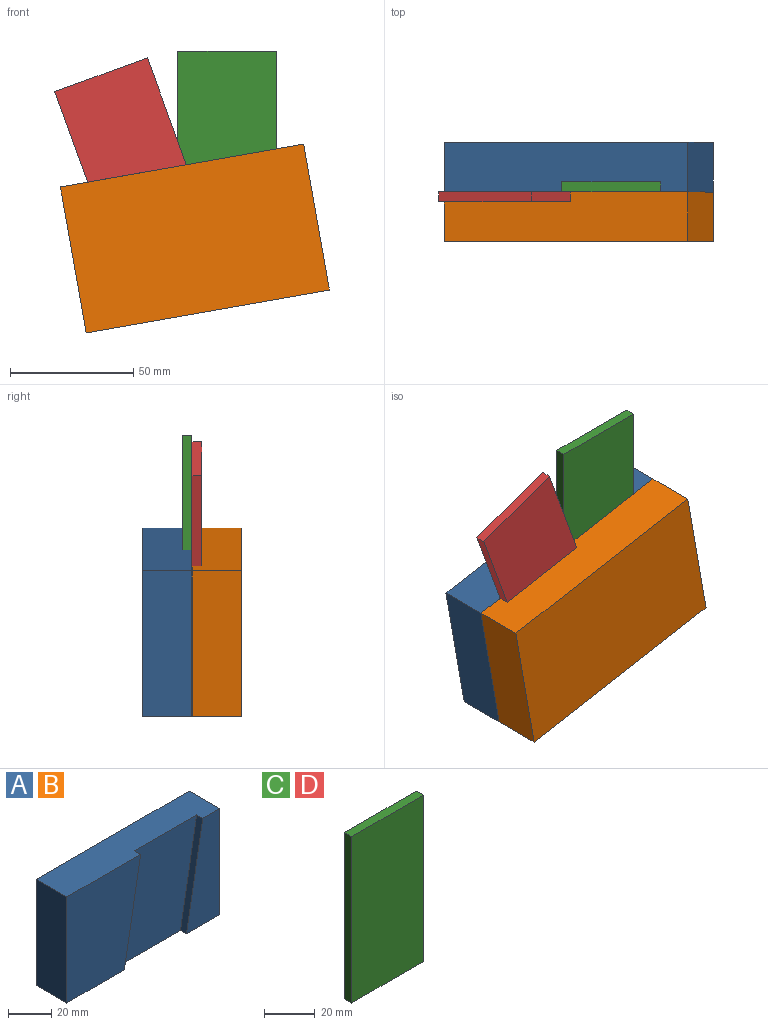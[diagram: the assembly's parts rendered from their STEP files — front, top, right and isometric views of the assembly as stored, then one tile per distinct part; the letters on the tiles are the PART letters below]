
ASSEMBLY  parts=4 mates=7
PART A: 10 faces, bbox 100x20x60 mm
  f0: plane 60x21.73mm, normal (0,-1,0), area 986.2mm2, adj f2,f4,f5,f7
  f1: plane 60x48.24mm, normal (0,-1,0), area 2576.8mm2, adj f2,f3,f4,f8
  f2: plane 100x20mm, normal (0,0,1), area 1837.5mm2, adj f0,f1,f3,f5,f6,f7,f8,f9
  f3: plane 60x20mm, normal (-1,0,0), area 1200mm2, adj f1,f2,f4,f6
  f4: plane 100x20mm, normal (0,0,-1), area 1837.5mm2, adj f0,f1,f3,f5,f6,f7,f8,f9
  f5: plane 60x20mm, normal (1,0,0), area 1200mm2, adj f0,f2,f4,f6
  f6: plane 100x60mm, normal (0,1,0), area 6000mm2, adj f2,f3,f4,f5
  f7: plane 60x10.58mm, normal (-0.98,0,0.17), area 243.7mm2, adj f0,f2,f4,f9
  f8: plane 60x10.58mm, normal (0.98,0,-0.17), area 243.7mm2, adj f1,f2,f4,f9
  f9: plane 60x51.2mm, normal (0,-1,0), area 2437mm2, adj f2,f4,f7,f8
PART B: same geometry as A
PART C: 6 faces, bbox 40x4x80 mm
  f0: plane 80x4mm, normal (-1,0,0), area 320mm2, adj f1,f3,f4,f5
  f1: plane 40x4mm, normal (0,0,-1), area 160mm2, adj f0,f2,f4,f5
  f2: plane 80x4mm, normal (1,0,0), area 320mm2, adj f1,f3,f4,f5
  f3: plane 40x4mm, normal (0,0,1), area 160mm2, adj f0,f2,f4,f5
  f4: plane 80x40mm, normal (0,-1,0), area 3200mm2, adj f0,f1,f2,f3
  f5: plane 80x40mm, normal (0,1,0), area 3200mm2, adj f0,f1,f2,f3
PART D: same geometry as C
PLACE A rot(axis=(0,-1,0),10deg) t=(-152.12,-78.45,-85.41)mm
PLACE B rot(axis=(0.09,0,-1),180deg) t=(-152.12,-118.45,-85.41)mm
PLACE C t=(-133.85,-94.45,-79.08)mm
PLACE D rot(axis=(0,1,0),160deg) t=(-171.25,-98.45,-86.25)mm
MATE planar A.f8 <-> C.f0  axis (1,0,0) through (-153.85,-96.45,-116.18)mm
MATE planar C.f4 <-> A.f1  axis (0,-1,0) through (-133.85,-98.45,-79.08)mm
MATE planar B.f4 <-> A.f4  axis (0.17,0,-0.98) through (-169.54,-102.45,-149.41)mm
MATE planar D.f4 <-> B.f9  axis (0,-1,0) through (-171.25,-102.45,-86.25)mm
MATE planar B.f5 <-> A.f3  axis (-0.98,0,-0.17) through (-190.94,-108.45,-153.18)mm
MATE planar B.f8 <-> D.f0  axis (-0.94,0,-0.34) through (-139.96,-100.45,-113.73)mm
MATE planar B.f1 <-> A.f1  axis (0,1,0) through (-119.14,-98.45,-108.81)mm
